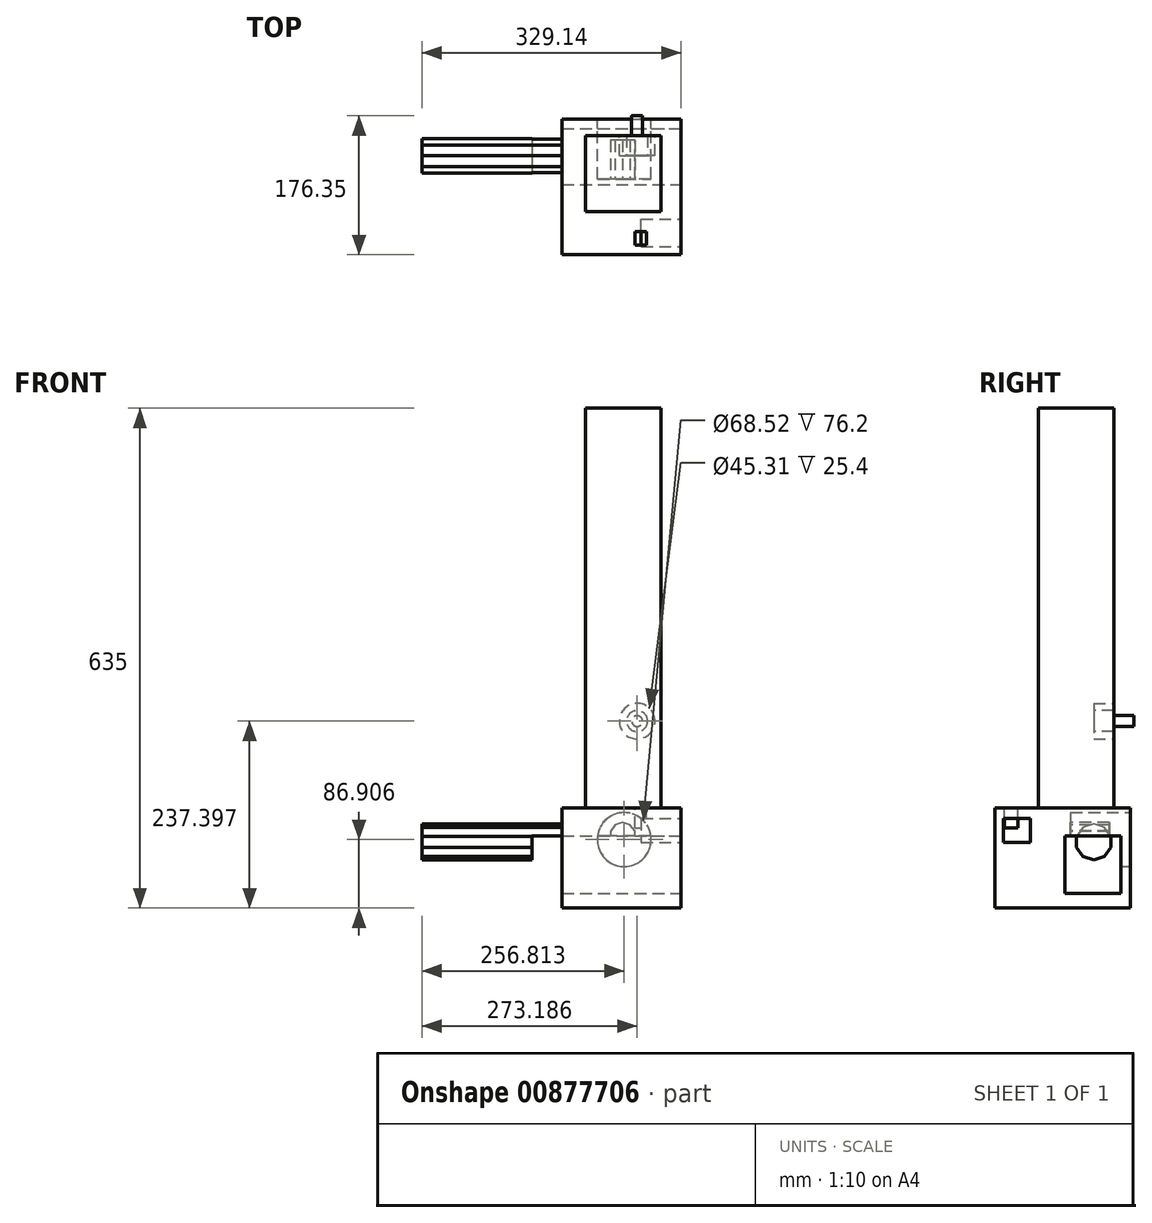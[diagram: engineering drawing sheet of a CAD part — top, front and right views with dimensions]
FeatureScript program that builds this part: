
annotation { "Feature Type Name" : "Feature", "Feature Type Description" : "" }
export const myFeature = defineFeature(function(context is Context, id is Id, definition is map)
    precondition{}
    {
        {
            var Q0;
            Q0=qCreatedBy(makeId("Top.planeOp"),FACE);
            var sketch = newSketch(context, id + "F0", { "sketchPlane" : qUnion([Q0])});
            skLineSegment(sketch, "E0.bottom", {"start": v(-72.3, 0) * mm, "end": v(79.04, 0) * mm});
            skLineSegment(sketch, "E0.top", {"start": v(-72.3, -172.12) * mm, "end": v(79.04, -172.12) * mm});
            skLineSegment(sketch, "E0.left", {"start": v(-72.3, 0) * mm, "end": v(-72.3, -172.12) * mm});
            skLineSegment(sketch, "E0.right", {"start": v(79.04, 0) * mm, "end": v(79.04, -172.12) * mm});
            skSolve(sketch);
        }
        {
            var Q0;
            Q0 = qSketchRegion(id + "F0", true);
            extrude(context, id + "F1", {"entities" : qUnion([Q0]), "depth" : 127 * mm, "offsetDistance" : 25.4 * mm});
        }
        {
            var Q0;
            Q0=makeQuery(id+"F1.opExtrude","SWEPT_FACE",FACE,{"disambiguationData":[OSD([sQuery(id+"F0.wireOp",EDGE,"E0.right")])]});
            var sketch = newSketch(context, id + "F2", { "sketchPlane" : qUnion([Q0])});
            skSolve(sketch);
        }
        {
            var Q0;
            {var subQ0=sQuery(id+"F0.wireOp",EDGE,"E0.right");Q0=makeQuery(id+"F2.imprint","IMPRINT",FACE,{"disambiguationData":[TD([[makeQuery(id+"F2.imprint","IMPRINT",EDGE,{"derivedFrom":makeQuery(id+"F1.opExtrude","CAP_EDGE",EDGE,{"disambiguationData":[OSD([subQ0])],"isStart":true})}),-1.0]])]});}
            var sketch = newSketch(context, id + "F3", { "sketchPlane" : qUnion([Q0])});
            skLineSegment(sketch, "E1.bottom", {"start": v(-161.63, 113.65) * mm, "end": v(-126.85, 113.65) * mm});
            skLineSegment(sketch, "E1.top", {"start": v(-161.63, 83.34) * mm, "end": v(-126.85, 83.34) * mm});
            skLineSegment(sketch, "E1.left", {"start": v(-161.63, 113.65) * mm, "end": v(-161.63, 83.34) * mm});
            skLineSegment(sketch, "E1.right", {"start": v(-126.85, 113.65) * mm, "end": v(-126.85, 83.34) * mm});
            skSolve(sketch);
        }
        {
            var Q0;
            Q0 = qSketchRegion(id + "F3", true);
            extrude(context, id + "F4", {"entities" : qUnion([Q0]), "operationType" : NewBodyOperationType.REMOVE, "oppositeDirection" : true, "depth" : 50.8 * mm, "offsetDistance" : 25.4 * mm});
        }
        {
            var Q0;
            Q0=makeQuery(id+"F1.opExtrude","CAP_FACE",FACE,{"disambiguationData":[OSD([sQuery(id+"F0.wireOp",EDGE,"E0.bottom"),sQuery(id+"F0.wireOp",EDGE,"E0.top"),sQuery(id+"F0.wireOp",EDGE,"E0.left"),sQuery(id+"F0.wireOp",EDGE,"E0.right")])],"isStart":false});
            var sketch = newSketch(context, id + "F5", { "sketchPlane" : qUnion([Q0])});
            skLineSegment(sketch, "E2.bottom", {"start": v(20.09, -160.3) * mm, "end": v(34.8, -160.3) * mm});
            skLineSegment(sketch, "E2.top", {"start": v(20.09, -142.9) * mm, "end": v(34.8, -142.9) * mm});
            skLineSegment(sketch, "E2.left", {"start": v(20.09, -160.3) * mm, "end": v(20.09, -142.9) * mm});
            skLineSegment(sketch, "E2.right", {"start": v(34.8, -160.3) * mm, "end": v(34.8, -142.9) * mm});
            skSolve(sketch);
        }
        {
            var Q0;
            Q0 = qSketchRegion(id + "F5", true);
            extrude(context, id + "F6", {"entities" : qUnion([Q0]), "operationType" : NewBodyOperationType.REMOVE, "oppositeDirection" : true, "depth" : 25.4 * mm, "offsetDistance" : 25.4 * mm});
        }
        {
            var Q0;
            Q0=makeQuery(id+"F1.opExtrude","SWEPT_FACE",FACE,{"disambiguationData":[OSD([sQuery(id+"F0.wireOp",EDGE,"E0.bottom")])]});
            var sketch = newSketch(context, id + "F7", { "sketchPlane" : qUnion([Q0])});
            skCircle(sketch, "E3", {"center": v(-6.71, 86.9) * mm, "radius": 34.26 * mm});
            skSolve(sketch);
        }
        {
            var Q0;
            Q0 = qSketchRegion(id + "F7", true);
            extrude(context, id + "F8", {"entities" : qUnion([Q0]), "operationType" : NewBodyOperationType.REMOVE, "oppositeDirection" : true, "depth" : 76.2 * mm, "offsetDistance" : 25.4 * mm});
        }
        {
            var Q0;
            Q0=makeQuery(id+"F1.opExtrude","SWEPT_FACE",FACE,{"disambiguationData":[OSD([sQuery(id+"F0.wireOp",EDGE,"E0.left")])]});
            var sketch = newSketch(context, id + "F9", { "sketchPlane" : qUnion([Q0])});
            skCircle(sketch, "E4.cCircle", {"center": v(46.6, 83.78) * mm, "radius": 21.85 * mm, "construction": true});
            skLineSegment(sketch, "E4.0", {"start": v(68.45, 90.88) * mm, "end": v(68.45, 76.69) * mm});
            skLineSegment(sketch, "E4.1", {"start": v(68.45, 76.69) * mm, "end": v(60.1, 65.2) * mm});
            skLineSegment(sketch, "E4.2", {"start": v(60.1, 65.2) * mm, "end": v(46.6, 60.82) * mm});
            skLineSegment(sketch, "E4.3", {"start": v(46.6, 60.82) * mm, "end": v(33.1, 65.2) * mm});
            skLineSegment(sketch, "E4.4", {"start": v(33.1, 65.2) * mm, "end": v(24.76, 76.69) * mm});
            skLineSegment(sketch, "E4.5", {"start": v(24.76, 76.69) * mm, "end": v(24.76, 90.88) * mm});
            skLineSegment(sketch, "E4.6", {"start": v(24.76, 90.88) * mm, "end": v(33.1, 102.37) * mm});
            skLineSegment(sketch, "E4.7", {"start": v(33.1, 102.37) * mm, "end": v(46.6, 106.75) * mm});
            skLineSegment(sketch, "E4.8", {"start": v(46.6, 106.75) * mm, "end": v(60.1, 102.37) * mm});
            skLineSegment(sketch, "E4.9", {"start": v(60.1, 102.37) * mm, "end": v(68.45, 90.88) * mm});
            skPoint(sketch, "E4.0.midPoint", {"position": v(68.45, 83.78) * mm});
            skSolve(sketch);
        }
        {
            var Q0;
            Q0 = qSketchRegion(id + "F9", true);
            extrude(context, id + "F10", {"entities" : qUnion([Q0]), "operationType" : NewBodyOperationType.ADD, "depth" : 177.8 * mm, "offsetDistance" : 25.4 * mm});
        }
        {
            var Q0;
            Q0=makeQuery(id+"F8.boolean.opBoolean","COPY",FACE,{"derivedFrom":makeQuery(id+"F8.opExtrude","CAP_FACE",FACE,{"disambiguationData":[OSD([sQuery(id+"F7.wireOp",EDGE,"E3")])],"isStart":false})});
            var sketch = newSketch(context, id + "F11", { "sketchPlane" : qUnion([Q0])});
            skSolve(sketch);
        }
        {
            var Q0;
            Q0=makeQuery(id+"F11.imprint","IMPRINT",FACE,{"disambiguationData":[TD([[makeQuery(id+"F11.imprint","IMPRINT",EDGE,{"derivedFrom":makeQuery(id+"F8.boolean.opBoolean","COPY",EDGE,{"derivedFrom":makeQuery(id+"F8.opExtrude","CAP_EDGE",EDGE,{"disambiguationData":[OSD([sQuery(id+"F7.wireOp",EDGE,"E3")])],"isStart":false})})}),1.0]])]});
            var sketch = newSketch(context, id + "F12", { "sketchPlane" : qUnion([Q0])});
            skCircle(sketch, "E5.cCircle", {"center": v(-4.71, 92.43) * mm, "radius": 15.57 * mm, "construction": true});
            skLineSegment(sketch, "E5.0", {"start": v(10.8, 87.22) * mm, "end": v(4.77, 79.1) * mm});
            skLineSegment(sketch, "E5.1", {"start": v(4.77, 79.1) * mm, "end": v(-4.88, 76.07) * mm});
            skLineSegment(sketch, "E5.2", {"start": v(-4.88, 76.07) * mm, "end": v(-14.47, 79.29) * mm});
            skLineSegment(sketch, "E5.3", {"start": v(-14.47, 79.29) * mm, "end": v(-20.33, 87.53) * mm});
            skLineSegment(sketch, "E5.4", {"start": v(-20.33, 87.53) * mm, "end": v(-20.23, 97.65) * mm});
            skLineSegment(sketch, "E5.5", {"start": v(-20.23, 97.65) * mm, "end": v(-14.2, 105.77) * mm});
            skLineSegment(sketch, "E5.6", {"start": v(-14.2, 105.77) * mm, "end": v(-4.55, 108.8) * mm});
            skLineSegment(sketch, "E5.7", {"start": v(-4.55, 108.8) * mm, "end": v(5.04, 105.58) * mm});
            skLineSegment(sketch, "E5.8", {"start": v(5.04, 105.58) * mm, "end": v(10.9, 97.33) * mm});
            skLineSegment(sketch, "E5.9", {"start": v(10.9, 97.33) * mm, "end": v(10.8, 87.22) * mm});
            skPoint(sketch, "E5.0.midPoint", {"position": v(7.79, 83.15) * mm});
            skSolve(sketch);
        }
        {
            var Q0;
            Q0 = qSketchRegion(id + "F12", true);
            extrude(context, id + "F13", {"entities" : qUnion([Q0]), "operationType" : NewBodyOperationType.ADD, "depth" : 49.28 * mm, "offsetDistance" : 25.4 * mm});
        }
        {
            var Q0;
            {var subQ0=sQuery(id+"F0.wireOp",EDGE,"E0.right");Q0=makeQuery(id+"F2.imprint","IMPRINT",FACE,{"disambiguationData":[TD([[makeQuery(id+"F2.imprint","IMPRINT",EDGE,{"derivedFrom":makeQuery(id+"F1.opExtrude","CAP_EDGE",EDGE,{"disambiguationData":[OSD([subQ0])],"isStart":true})}),-1.0]])]});}
            var sketch = newSketch(context, id + "F14", { "sketchPlane" : qUnion([Q0])});
            skLineSegment(sketch, "E6.bottom", {"start": v(-83.3, 91.72) * mm, "end": v(-12.11, 91.72) * mm});
            skLineSegment(sketch, "E6.top", {"start": v(-83.3, 18.56) * mm, "end": v(-12.11, 18.56) * mm});
            skLineSegment(sketch, "E6.left", {"start": v(-83.3, 91.72) * mm, "end": v(-83.3, 18.56) * mm});
            skLineSegment(sketch, "E6.right", {"start": v(-12.11, 91.72) * mm, "end": v(-12.11, 18.56) * mm});
            skSolve(sketch);
        }
        {
            var Q0;
            Q0 = qSketchRegion(id + "F14", true);
            extrude(context, id + "F15", {"entities" : qUnion([Q0]), "operationType" : NewBodyOperationType.REMOVE, "oppositeDirection" : true, "depth" : 189.39 * mm, "offsetDistance" : 25.4 * mm});
        }
        {
            var Q0;
            Q0=makeQuery(id+"F1.opExtrude","CAP_FACE",FACE,{"disambiguationData":[OSD([sQuery(id+"F0.wireOp",EDGE,"E0.bottom"),sQuery(id+"F0.wireOp",EDGE,"E0.top"),sQuery(id+"F0.wireOp",EDGE,"E0.left"),sQuery(id+"F0.wireOp",EDGE,"E0.right")])],"isStart":false});
            var sketch = newSketch(context, id + "F16", { "sketchPlane" : qUnion([Q0])});
            skLineSegment(sketch, "E7.bottom", {"start": v(-42.27, -21.17) * mm, "end": v(53.23, -21.17) * mm});
            skLineSegment(sketch, "E7.top", {"start": v(-42.27, -117.19) * mm, "end": v(53.23, -117.19) * mm});
            skLineSegment(sketch, "E7.left", {"start": v(-42.27, -21.17) * mm, "end": v(-42.27, -117.19) * mm});
            skLineSegment(sketch, "E7.right", {"start": v(53.23, -21.17) * mm, "end": v(53.23, -117.19) * mm});
            skSolve(sketch);
        }
        {
            var Q0;
            Q0 = qSketchRegion(id + "F16", true);
            extrude(context, id + "F17", {"entities" : qUnion([Q0]), "operationType" : NewBodyOperationType.ADD, "depth" : 508 * mm, "offsetDistance" : 25.4 * mm});
        }
        {
            var Q0;
            Q0=makeQuery(id+"F17.opExtrude","SWEPT_FACE",FACE,{"disambiguationData":[OSD([sQuery(id+"F16.wireOp",EDGE,"E7.bottom")])]});
            var sketch = newSketch(context, id + "F18", { "sketchPlane" : qUnion([Q0])});
            skCircle(sketch, "E8", {"center": v(-23.09, 237.4) * mm, "radius": 22.66 * mm});
            skSolve(sketch);
        }
        {
            var Q0;
            Q0 = qSketchRegion(id + "F18", true);
            extrude(context, id + "F19", {"entities" : qUnion([Q0]), "operationType" : NewBodyOperationType.REMOVE, "oppositeDirection" : true, "depth" : 25.4 * mm, "offsetDistance" : 25.4 * mm});
        }
        {
            var Q0;
            Q0=makeQuery(id+"F19.boolean.opBoolean","COPY",FACE,{"derivedFrom":makeQuery(id+"F19.opExtrude","CAP_FACE",FACE,{"disambiguationData":[OSD([sQuery(id+"F18.wireOp",EDGE,"E8")])],"isStart":false})});
            var sketch = newSketch(context, id + "F20", { "sketchPlane" : qUnion([Q0])});
            skCircle(sketch, "E9", {"center": v(-23.09, 237.4) * mm, "radius": 12.5 * mm});
            skSolve(sketch);
        }
        {
            var Q0;
            Q0 = qSketchRegion(id + "F20", true);
            extrude(context, id + "F21", {"entities" : qUnion([Q0]), "operationType" : NewBodyOperationType.ADD, "oppositeDirection" : true, "depth" : 25.4 * mm, "offsetDistance" : 25.4 * mm});
        }
        {
            var Q0;
            Q0=makeQuery(id+"F19.boolean.opBoolean","COPY",FACE,{"derivedFrom":makeQuery(id+"F19.opExtrude","CAP_FACE",FACE,{"disambiguationData":[OSD([sQuery(id+"F18.wireOp",EDGE,"E8")])],"isStart":false})});
            var sketch = newSketch(context, id + "F22", { "sketchPlane" : qUnion([Q0])});
            skCircle(sketch, "E10", {"center": v(-23.09, 237.4) * mm, "radius": 13.34 * mm});
            skSolve(sketch);
        }
        {
            var Q0;
            Q0 = qSketchRegion(id + "F22", true);
            extrude(context, id + "F23", {"entities" : qUnion([Q0]), "operationType" : NewBodyOperationType.ADD, "depth" : 25.4 * mm, "offsetDistance" : 25.4 * mm});
        }
        {
            var Q0;
            Q0=makeQuery(id+"F23.opExtrude","CAP_FACE",FACE,{"disambiguationData":[OSD([sQuery(id+"F22.wireOp",EDGE,"E10")])],"isStart":false});
            var sketch = newSketch(context, id + "F24", { "sketchPlane" : qUnion([Q0])});
            skCircle(sketch, "E11", {"center": v(-23.09, 237.4) * mm, "radius": 6.92 * mm});
            skSolve(sketch);
        }
        {
            var Q0;
            Q0 = qSketchRegion(id + "F24", true);
            extrude(context, id + "F25", {"entities" : qUnion([Q0]), "operationType" : NewBodyOperationType.ADD, "depth" : 25.4 * mm, "offsetDistance" : 25.4 * mm});
        }
    });
